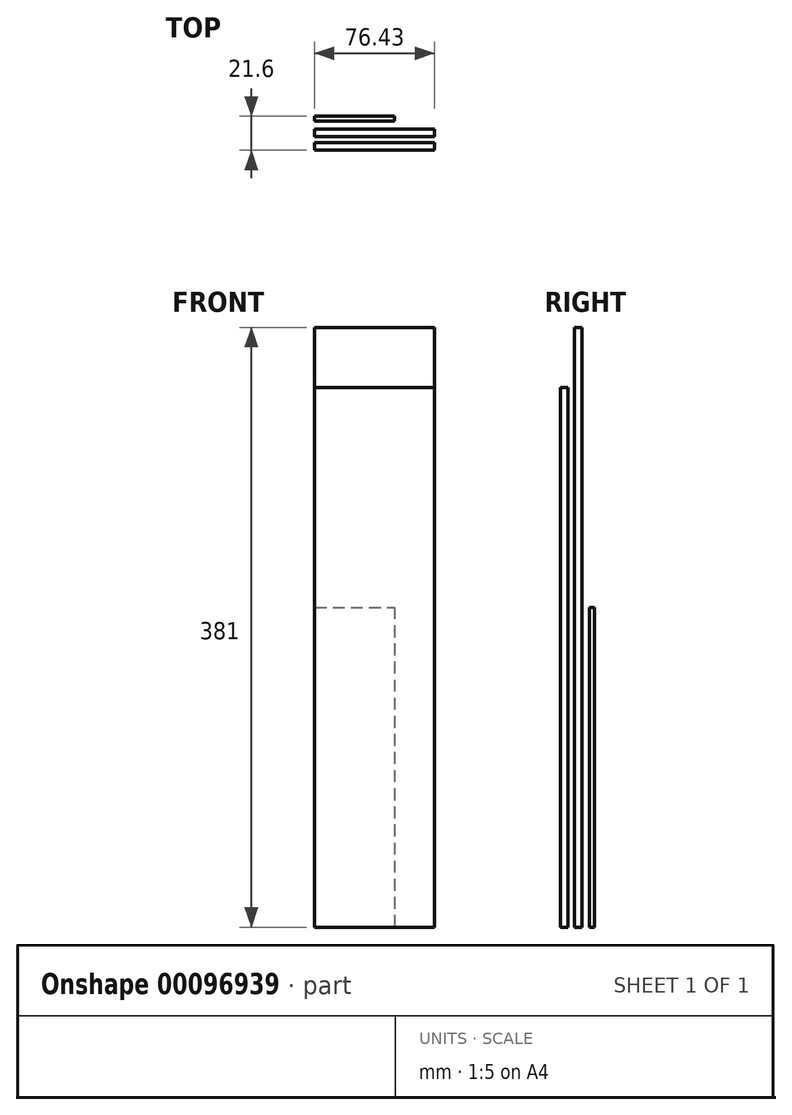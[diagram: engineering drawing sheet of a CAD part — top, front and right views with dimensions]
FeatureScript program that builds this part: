
annotation { "Feature Type Name" : "Feature", "Feature Type Description" : "" }
export const myFeature = defineFeature(function(context is Context, id is Id, definition is map)
    precondition{}
    {
        {
            var Q0;
            Q0=qCreatedBy(makeId("Top.planeOp"),FACE);
            var sketch = newSketch(context, id + "F0", { "sketchPlane" : qUnion([Q0])});
            skLineSegment(sketch, "E0.bottom", {"start": v(0, 0) * mm, "end": v(50.8, 0) * mm});
            skLineSegment(sketch, "E0.top", {"start": v(0, 3.18) * mm, "end": v(50.8, 3.18) * mm});
            skLineSegment(sketch, "E0.left", {"start": v(0, 0) * mm, "end": v(0, 3.18) * mm});
            skLineSegment(sketch, "E0.right", {"start": v(50.8, 0) * mm, "end": v(50.8, 3.18) * mm});
            skSolve(sketch);
        }
        {
            var Q0;
            Q0=makeQuery(id+"F0.imprint","IMPRINT",FACE,{"disambiguationData":[TD([[makeQuery(id+"F0.imprint","IMPRINT",EDGE,{"derivedFrom":sQuery(id+"F0.wireOp",EDGE,"E0.bottom")}),1.0]])]});
            extrude(context, id + "F1", {"entities" : qUnion([Q0]), "depth" : 203.2 * mm});
        }
        {
            var Q0;
            Q0=qCreatedBy(makeId("Top.planeOp"),FACE);
            var sketch = newSketch(context, id + "F2", { "sketchPlane" : qUnion([Q0])});
            skLineSegment(sketch, "E1.bottom", {"start": v(0, -13.67) * mm, "end": v(76.2, -13.67) * mm});
            skLineSegment(sketch, "E1.top", {"start": v(0, -18.43) * mm, "end": v(76.2, -18.43) * mm});
            skLineSegment(sketch, "E1.left", {"start": v(0, -13.67) * mm, "end": v(0, -18.43) * mm});
            skLineSegment(sketch, "E1.right", {"start": v(76.2, -13.67) * mm, "end": v(76.2, -18.43) * mm});
            skSolve(sketch);
        }
        {
            var Q0;
            Q0 = qSketchRegion(id + "F2", true);
            extrude(context, id + "F3", {"entities" : qUnion([Q0]), "depth" : 342.9 * mm});
        }
        {
            var Q0;
            Q0=qCreatedBy(makeId("Top.planeOp"),FACE);
            var sketch = newSketch(context, id + "F4", { "sketchPlane" : qUnion([Q0])});
            skLineSegment(sketch, "E2.bottom", {"start": v(-0.23, -4.84) * mm, "end": v(75.97, -4.84) * mm});
            skLineSegment(sketch, "E2.top", {"start": v(-0.23, -9.6) * mm, "end": v(75.97, -9.6) * mm});
            skLineSegment(sketch, "E2.left", {"start": v(-0.23, -4.84) * mm, "end": v(-0.23, -9.6) * mm});
            skLineSegment(sketch, "E2.right", {"start": v(75.97, -4.84) * mm, "end": v(75.97, -9.6) * mm});
            skSolve(sketch);
        }
        {
            var Q0;
            Q0=makeQuery(id+"F4.imprint","IMPRINT",FACE,{"disambiguationData":[TD([[makeQuery(id+"F4.imprint","IMPRINT",EDGE,{"derivedFrom":sQuery(id+"F4.wireOp",EDGE,"E2.bottom")}),-1.0]])]});
            extrude(context, id + "F5", {"entities" : qUnion([Q0]), "depth" : 381 * mm});
        }
    });
